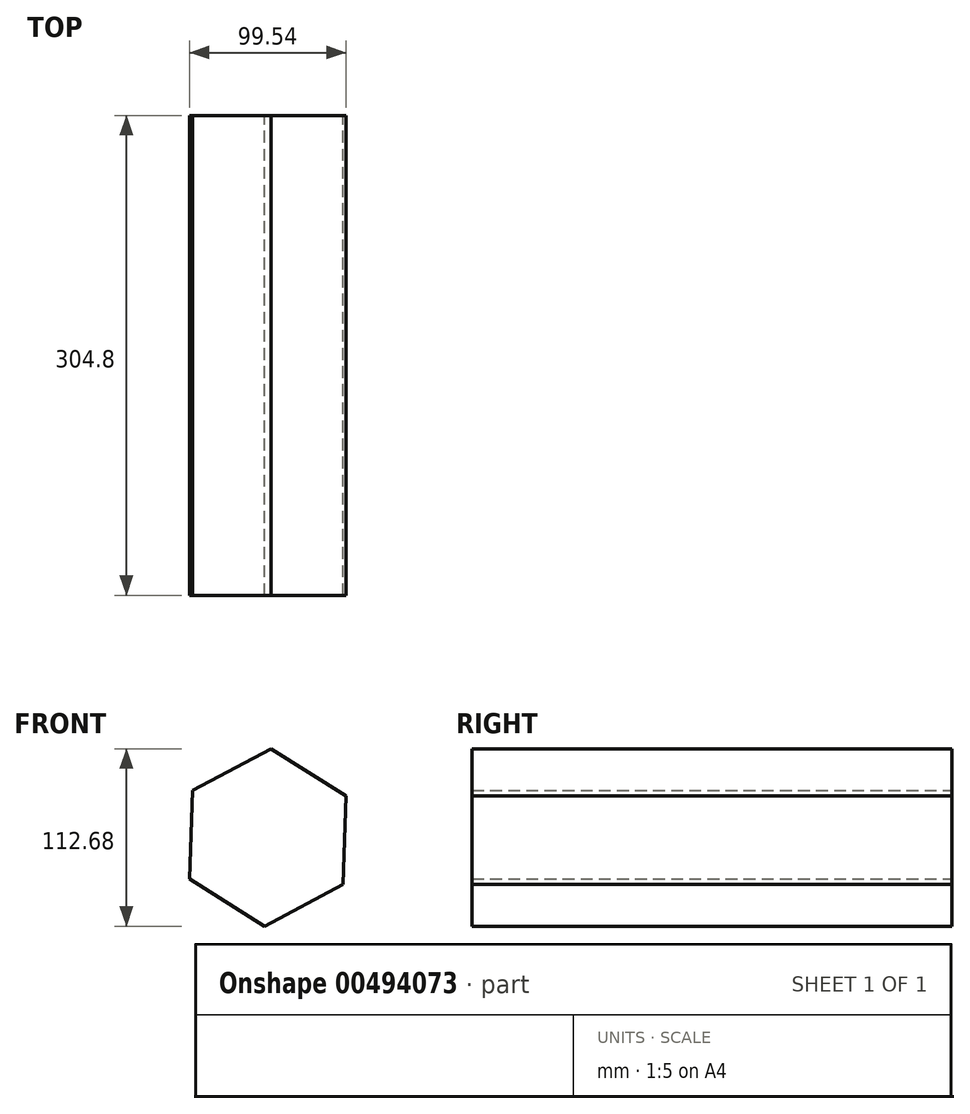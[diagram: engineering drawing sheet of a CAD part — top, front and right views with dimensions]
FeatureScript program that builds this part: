
annotation { "Feature Type Name" : "Feature", "Feature Type Description" : "" }
export const myFeature = defineFeature(function(context is Context, id is Id, definition is map)
    precondition{}
    {
        {
            var Q0;
            Q0=qCreatedBy(makeId("Front.planeOp"),FACE);
            var sketch = newSketch(context, id + "F0", { "sketchPlane" : qUnion([Q0])});
            skCircle(sketch, "E0.cCircle", {"center": v(0, 0) * mm, "radius": 56.37 * mm, "construction": true});
            skLineSegment(sketch, "E0.0", {"start": v(-47.8, 29.88) * mm, "end": v(1.97, 56.34) * mm});
            skLineSegment(sketch, "E0.1", {"start": v(1.97, 56.34) * mm, "end": v(49.77, 26.46) * mm});
            skLineSegment(sketch, "E0.2", {"start": v(49.77, 26.46) * mm, "end": v(47.8, -29.88) * mm});
            skLineSegment(sketch, "E0.3", {"start": v(47.8, -29.88) * mm, "end": v(-1.97, -56.34) * mm});
            skLineSegment(sketch, "E0.4", {"start": v(-1.97, -56.34) * mm, "end": v(-49.77, -26.46) * mm});
            skLineSegment(sketch, "E0.5", {"start": v(-49.77, -26.46) * mm, "end": v(-47.8, 29.88) * mm});
            skSolve(sketch);
        }
        {
            var Q0;
            Q0=makeQuery(id+"F0.imprint","IMPRINT",FACE,{"disambiguationData":[TD([[makeQuery(id+"F0.imprint","IMPRINT",EDGE,{"derivedFrom":sQuery(id+"F0.wireOp",EDGE,"E0.0")}),-1.0]])]});
            extrude(context, id + "F1", {"entities" : qUnion([Q0]), "depth" : 304.8 * mm});
        }
    });
